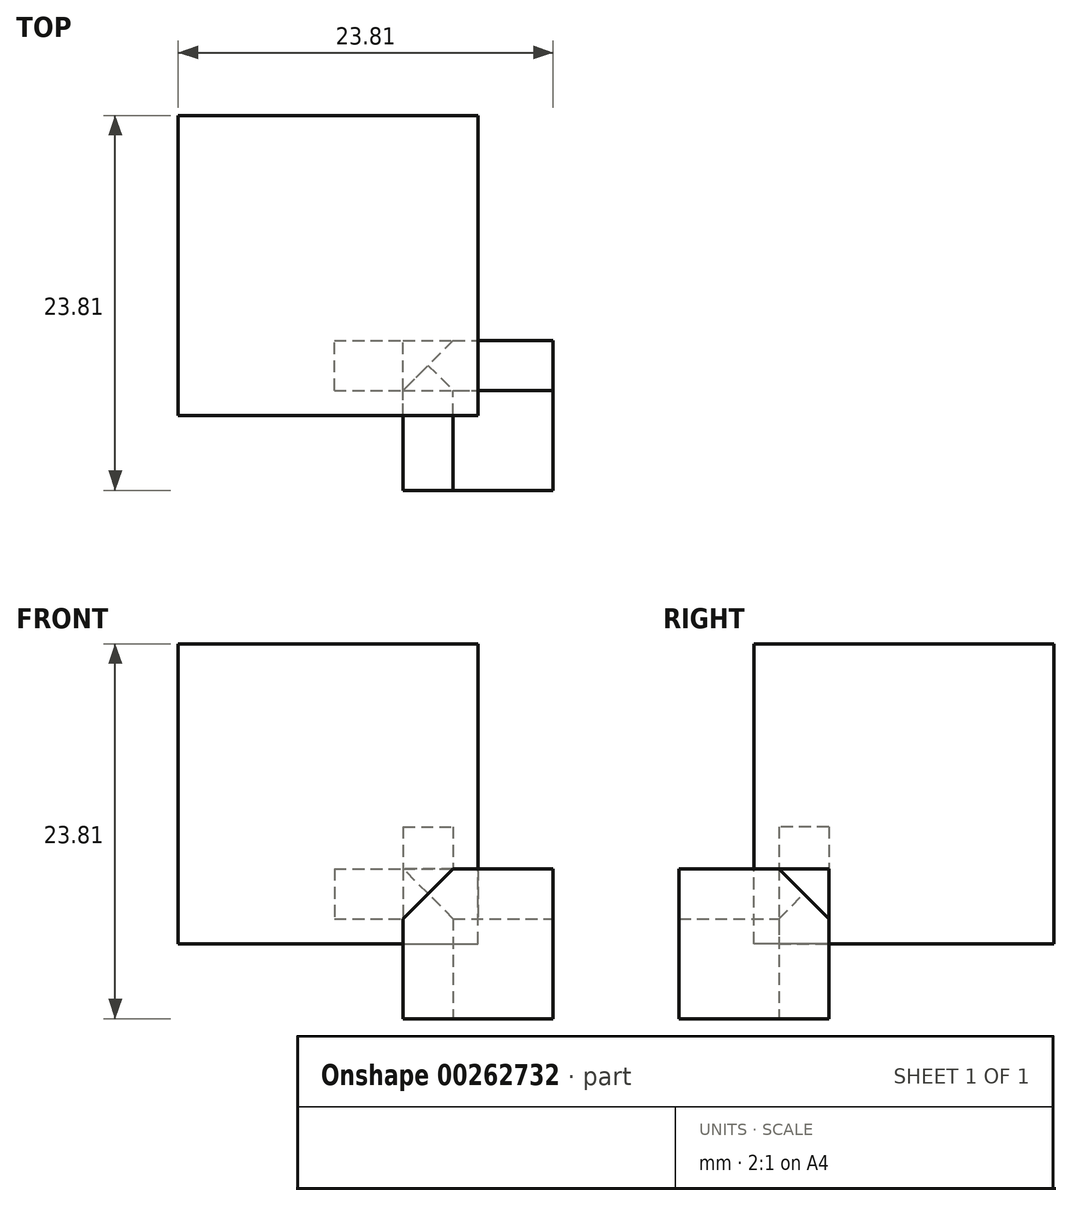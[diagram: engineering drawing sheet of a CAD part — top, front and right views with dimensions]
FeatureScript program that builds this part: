
annotation { "Feature Type Name" : "Feature", "Feature Type Description" : "" }
export const myFeature = defineFeature(function(context is Context, id is Id, definition is map)
    precondition{}
    {
        {
            var Q0;
            Q0=qCreatedBy(makeId("Front.planeOp"),FACE);
            var sketch = newSketch(context, id + "F0", { "sketchPlane" : qUnion([Q0])});
            skLineSegment(sketch, "E0.bottom", {"start": v(0, 0) * mm, "end": v(19.05, 0) * mm});
            skLineSegment(sketch, "E0.top", {"start": v(0, 19.05) * mm, "end": v(19.05, 19.05) * mm});
            skLineSegment(sketch, "E0.left", {"start": v(0, 0) * mm, "end": v(0, 19.05) * mm});
            skLineSegment(sketch, "E0.right", {"start": v(19.05, 0) * mm, "end": v(19.05, 19.05) * mm});
            skSolve(sketch);
        }
        {
            var Q0;
            Q0 = qSketchRegion(id + "F0", true);
            extrude(context, id + "F1", {"entities" : qUnion([Q0]), "oppositeDirection" : true, "depth" : 19.05 * mm});
        }
        {
            var Q0;
            Q0=makeQuery(id+"F1.opExtrude","CAP_FACE",FACE,{"disambiguationData":[OSD([sQuery(id+"F0.wireOp",EDGE,"E0.bottom"),sQuery(id+"F0.wireOp",EDGE,"E0.top"),sQuery(id+"F0.wireOp",EDGE,"E0.left"),sQuery(id+"F0.wireOp",EDGE,"E0.right")])],"isStart":true});
            cPlane(context, id + "F2", {"entities" : qUnion([Q0]), "cplaneType" : CPlaneType.OFFSET, "offset" : 4.76 * mm, "oppositeDirection" : true, "width" : 152.4 * mm, "height" : 152.4 * mm});
        }
        {
            var Q0;
            Q0=qCreatedBy(id+"F2.planeOp",FACE);
            var sketch = newSketch(context, id + "F3", { "sketchPlane" : qUnion([Q0])});
            skLineSegment(sketch, "E1.bottom", {"start": v(17.46, 4.76) * mm, "end": v(23.81, 4.76) * mm});
            skLineSegment(sketch, "E1.top", {"start": v(14.29, -4.76) * mm, "end": v(23.81, -4.76) * mm});
            skLineSegment(sketch, "E1.left", {"start": v(14.29, 1.59) * mm, "end": v(14.29, -4.76) * mm});
            skLineSegment(sketch, "E1.right", {"start": v(23.81, 4.76) * mm, "end": v(23.81, -4.76) * mm});
            skLineSegment(sketch, "E2", {"start": v(14.29, 1.59) * mm, "end": v(17.46, 4.76) * mm});
            skPoint(sketch, "E3", {"position": v(19.05, 0) * mm});
            skPoint(sketch, "E3.positionSnap0", {"position": v(19.05, -4.76) * mm});
            skPoint(sketch, "E3.positionSnap1", {"position": v(23.81, 0) * mm});
            skSolve(sketch);
        }
        {
            var Q0;
            Q0 = qSketchRegion(id + "F3", true);
            extrude(context, id + "F4", {"entities" : qUnion([Q0]), "depth" : 9.52 * mm});
        }
        {
            var Q0;
            Q0=makeQuery(id+"F4.opExtrude","SWEPT_FACE",FACE,{"disambiguationData":[OSD([sQuery(id+"F3.wireOp",EDGE,"E1.right")])]});
            var sketch = newSketch(context, id + "F5", { "sketchPlane" : qUnion([Q0])});
            skLineSegment(sketch, "E4", {"start": v(1.59, 4.76) * mm, "end": v(4.76, 1.59) * mm});
            skLineSegment(sketch, "E5", {"start": v(4.76, 1.59) * mm, "end": v(4.76, 4.76) * mm});
            skLineSegment(sketch, "E6", {"start": v(4.76, 4.76) * mm, "end": v(1.59, 4.76) * mm});
            skSolve(sketch);
        }
        {
            var Q0;
            Q0 = qSketchRegion(id + "F5", true);
            extrude(context, id + "F6", {"entities" : qUnion([Q0]), "operationType" : NewBodyOperationType.REMOVE, "oppositeDirection" : true, "depth" : 13.9 * mm});
        }
        {
            var Q0;
            Q0=makeQuery(id+"F4.opExtrude","SWEPT_FACE",FACE,{"disambiguationData":[OSD([sQuery(id+"F3.wireOp",EDGE,"E1.top")])]});
            var sketch = newSketch(context, id + "F7", { "sketchPlane" : qUnion([Q0])});
            skLineSegment(sketch, "E7", {"start": v(14.29, -4.76) * mm, "end": v(14.29, -1.59) * mm});
            skLineSegment(sketch, "E8", {"start": v(17.46, -4.76) * mm, "end": v(14.29, -4.76) * mm});
            skLineSegment(sketch, "E9", {"start": v(17.46, -4.76) * mm, "end": v(14.29, -1.59) * mm});
            skLineSegment(sketch, "E10", {"start": v(14.29, -4.76) * mm, "end": v(17.46, -4.76) * mm});
            skLineSegment(sketch, "E11", {"start": v(14.29, -1.59) * mm, "end": v(14.29, -4.76) * mm});
            skSolve(sketch);
        }
        {
            var Q0;
            Q0 = qSketchRegion(id + "F7", true);
            extrude(context, id + "F8", {"entities" : qUnion([Q0]), "operationType" : NewBodyOperationType.REMOVE, "oppositeDirection" : true, "depth" : 12.2 * mm});
        }
    });
